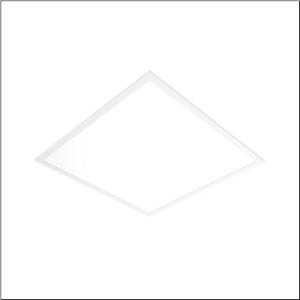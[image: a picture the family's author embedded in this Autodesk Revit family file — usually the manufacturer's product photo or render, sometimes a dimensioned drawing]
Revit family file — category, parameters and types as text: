
# Revit family: apollon_r__41_51mh12wd2443_fb74
name_source: partatom
category: Lighting Fixtures
units: mm (PartAtom-declared; Revit-internal decimal feet)

## family parameters
Cut with Voids When Loaded = No
Host = Face
Light Source = No
Part Type = Normal
Room Calculation Point = No
Round Connector Dimension = Use Diameter
Shared = No

## types (1)
- Apollon® 41 (1 x LED, 3500 lm, 28.5 W, 4000K)
    Apparent Load = 29 VA
    CIE Flux Codes = 61 87 97 100 100
    Color Rendering = 80
    Color Temperature = 4000K
    Default Elevation = 1800 mm
    Description = Apollon® 41, office luminaire, primary optical cover: prismatic diffuser, of PS, light emission: direct distribution, primary light characteristic: symmetric, installation type: lay-in mounting, LED, rated luminous flux: 3.500lm, luminous efficacy: 123lm/W, light colour: 840, colour temperature: 4000K, with terminal, 5-pole, mains connection: 220..240V, AC/DC, 0/50..60Hz, housing, of aluminium section, traffic white (RAL 9016), module: M600, length: 600mm, width: 600mm, height: 28mm, housing upper side, of sheet steel, protection rating (complete): IP20, protection rating (lamp compartment, on room side): IP40, insulation class (complete): insulation class II (safety insulation), certification: CE, ENEC, permissible operating ambient temperature: -25..+40°C, packaging unit: 1 piece
    Height = 0 mm  [stored 0 ft]
    Lamp = 1 x LED
    Lamp Light Flux = 3500 lm
    Lamp Power = 28.5 W
    Lamp count = 1
    Length = 600 mm
    Luminous efficacy = 123 lm/W
    Manufacturer = Siteco
    ModVariant = No
    Model = 51MH12WD2443
    Mounting Place = Ceiling
    Mounting Type = Recessed
    Number of Poles = 1
    OnlyDefault = Yes
    Power Factor = 1
    Product Name = Apollon® 41
    Product group = office luminaire | ceiling recessed
    ProductGroupID = 401
    Protection Class = Protection class II
    Protection Degree = IP 20
    RLX_Detail_Level = 1
    RLX_Emergency_Light_Flux = 0 lm
    RLX_Emergency_Type = 0
    RLX_Emergency_Type_DB = No
    RlxData = <blob elided: 12185 chars, md5=75f76d54>
    Socket = socket
    Standby Power = 0 W
    System Light Flux = 3500 lm
    System Power = 29 W
    Type Comments = Product without accessories
    Type Image = l_1291024.jpg
    URL = http://relux.com
    VarID = ---
    Voltage = 0 V
    Weight = 0.00 kg
    Width = 600 mm

note: [stored X ft] marks values corroborated as IEEE doubles in the binary element streams (Revit-internal decimal feet)

## geometry (parser evidence)
native form markers: Sweep x10
no freeform markers — native parametric forms only
